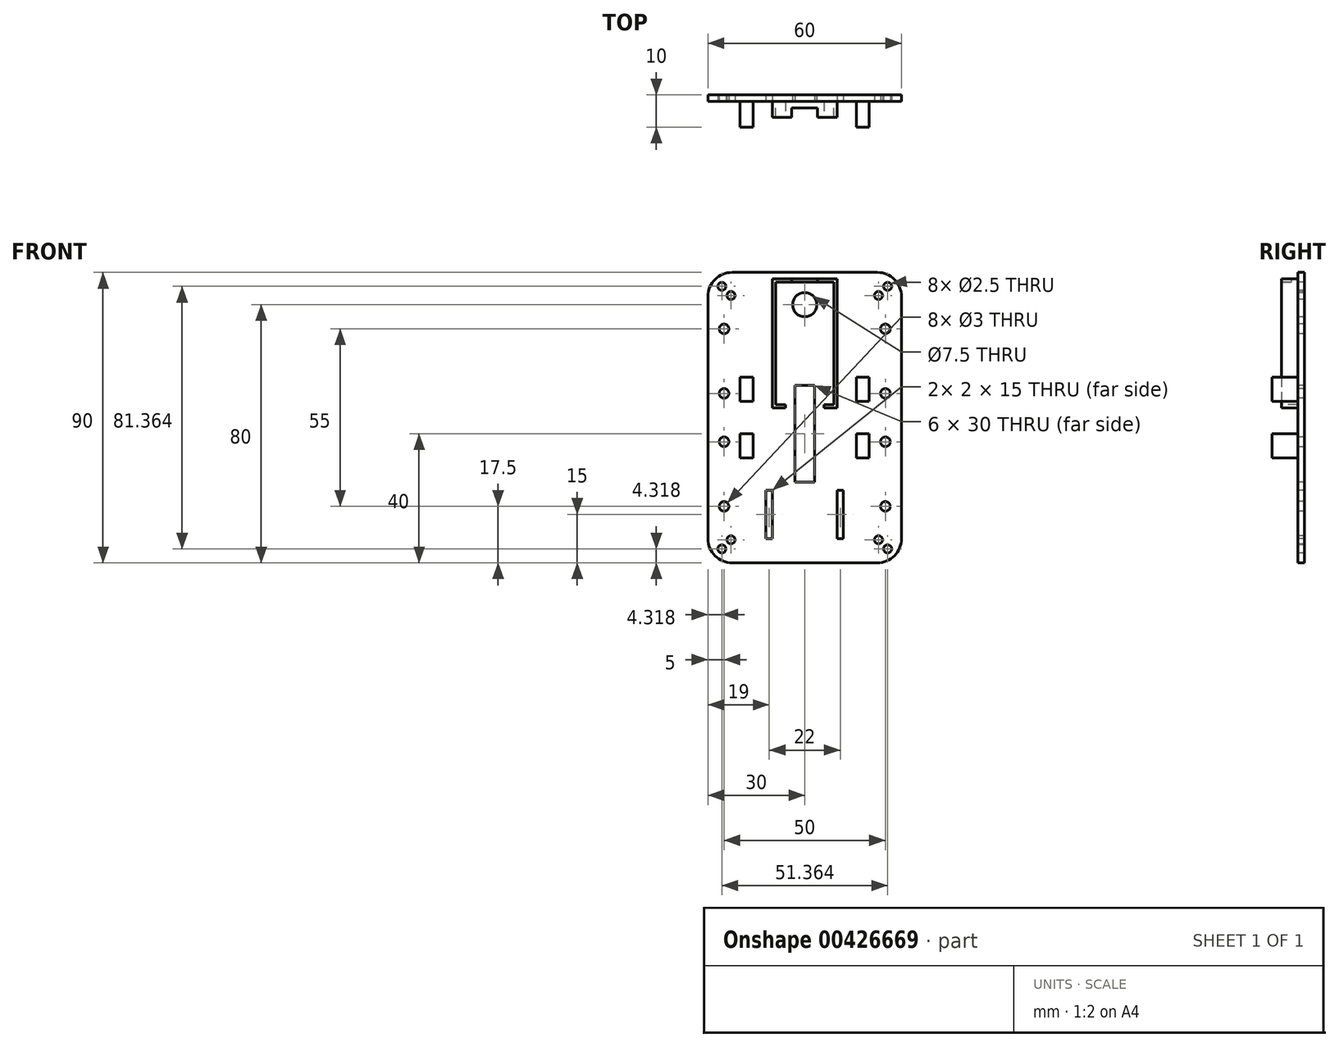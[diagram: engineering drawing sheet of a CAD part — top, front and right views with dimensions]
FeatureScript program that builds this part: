
annotation { "Feature Type Name" : "Feature", "Feature Type Description" : "" }
export const myFeature = defineFeature(function(context is Context, id is Id, definition is map)
    precondition{}
    {
        {
            var Q0;
            Q0=qCreatedBy(makeId("Front.planeOp"),FACE);
            var sketch = newSketch(context, id + "F0", { "sketchPlane" : qUnion([Q0])});
            skLineSegment(sketch, "E0.bottom", {"start": v(0, 0) * mm, "end": v(60, 0) * mm});
            skLineSegment(sketch, "E0.top", {"start": v(0, 90) * mm, "end": v(60, 90) * mm});
            skLineSegment(sketch, "E0.left", {"start": v(0, 0) * mm, "end": v(0, 90) * mm});
            skLineSegment(sketch, "E0.right", {"start": v(60, 0) * mm, "end": v(60, 90) * mm});
            skSolve(sketch);
        }
        {
            var Q0;
            Q0 = qSketchRegion(id + "F0", true);
            extrude(context, id + "F1", {"entities" : qUnion([Q0]), "depth" : 2 * mm, "offsetDistance" : 25 * mm});
        }
        {
            var Q0;
            Q0=makeQuery(id+"F1.opExtrude","SWEPT_EDGE",EDGE,{"disambiguationData":[OSD([sQuery(id+"F0.wireOp",EDGE,"E0.top"),sQuery(id+"F0.wireOp",EDGE,"E0.left")])]});
            var Q1;
            Q1=makeQuery(id+"F1.opExtrude","SWEPT_EDGE",EDGE,{"disambiguationData":[OSD([sQuery(id+"F0.wireOp",EDGE,"E0.top"),sQuery(id+"F0.wireOp",EDGE,"E0.right")])]});
            var Q2;
            Q2=makeQuery(id+"F1.opExtrude","SWEPT_EDGE",EDGE,{"disambiguationData":[OSD([sQuery(id+"F0.wireOp",EDGE,"E0.bottom"),sQuery(id+"F0.wireOp",EDGE,"E0.right")])]});
            var Q3;
            Q3=makeQuery(id+"F1.opExtrude","SWEPT_EDGE",EDGE,{"disambiguationData":[OSD([sQuery(id+"F0.wireOp",EDGE,"E0.bottom"),sQuery(id+"F0.wireOp",EDGE,"E0.left")])]});
            fillet(context, id + "F2", {"entities" : qUnion([Q0, Q1, Q2, Q3]), "radius" : 7.5 * mm, "tangentPropagation" : true, "allowEdgeOverflow" : false});
        }
        {
            var Q0;
            Q0=makeQuery(id+"F1.opExtrude","CAP_FACE",FACE,{"disambiguationData":[OSD([sQuery(id+"F0.wireOp",EDGE,"E0.bottom"),sQuery(id+"F0.wireOp",EDGE,"E0.top"),sQuery(id+"F0.wireOp",EDGE,"E0.left"),sQuery(id+"F0.wireOp",EDGE,"E0.right")])],"isStart":false});
            var sketch = newSketch(context, id + "F3", { "sketchPlane" : qUnion([Q0])});
            skSolve(sketch);
        }
        {
            var Q0;
            Q0=makeQuery(id+"F1.opExtrude","CAP_FACE",FACE,{"disambiguationData":[OSD([sQuery(id+"F0.wireOp",EDGE,"E0.bottom"),sQuery(id+"F0.wireOp",EDGE,"E0.top"),sQuery(id+"F0.wireOp",EDGE,"E0.left"),sQuery(id+"F0.wireOp",EDGE,"E0.right")])],"isStart":false});
            var sketch = newSketch(context, id + "F4", { "sketchPlane" : qUnion([Q0])});
            skLineSegment(sketch, "E1.bottom", {"start": v(18, 22.5) * mm, "end": v(20, 22.5) * mm});
            skLineSegment(sketch, "E1.top", {"start": v(18, 7.5) * mm, "end": v(20, 7.5) * mm});
            skLineSegment(sketch, "E1.left", {"start": v(18, 22.5) * mm, "end": v(18, 7.5) * mm});
            skLineSegment(sketch, "E1.right", {"start": v(20, 22.5) * mm, "end": v(20, 7.5) * mm});
            skLineSegment(sketch, "E2.bottom", {"start": v(42, 22.5) * mm, "end": v(40, 22.5) * mm});
            skLineSegment(sketch, "E2.top", {"start": v(42, 7.5) * mm, "end": v(40, 7.5) * mm});
            skLineSegment(sketch, "E2.left", {"start": v(42, 22.5) * mm, "end": v(42, 7.5) * mm});
            skLineSegment(sketch, "E2.right", {"start": v(40, 22.5) * mm, "end": v(40, 7.5) * mm});
            skSolve(sketch);
        }
        {
            var Q0;
            Q0 = qSketchRegion(id + "F4", true);
            extrude(context, id + "F5", {"entities" : qUnion([Q0]), "operationType" : NewBodyOperationType.REMOVE, "oppositeDirection" : true, "depth" : 25 * mm});
        }
        {
            var Q0;
            Q0=makeQuery(id+"F1.opExtrude","CAP_FACE",FACE,{"disambiguationData":[OSD([sQuery(id+"F0.wireOp",EDGE,"E0.bottom"),sQuery(id+"F0.wireOp",EDGE,"E0.top"),sQuery(id+"F0.wireOp",EDGE,"E0.left"),sQuery(id+"F0.wireOp",EDGE,"E0.right")])],"isStart":false});
            var sketch = newSketch(context, id + "F6", { "sketchPlane" : qUnion([Q0])});
            skLineSegment(sketch, "E3.bottom", {"start": v(21, 87) * mm, "end": v(39, 87) * mm});
            skLineSegment(sketch, "E3.top", {"start": v(21, 49) * mm, "end": v(39, 49) * mm});
            skLineSegment(sketch, "E3.left", {"start": v(21, 87) * mm, "end": v(21, 49) * mm});
            skLineSegment(sketch, "E3.right", {"start": v(39, 87) * mm, "end": v(39, 49) * mm});
            skLineSegment(sketch, "E4.bottom", {"start": v(20, 88) * mm, "end": v(40, 88) * mm});
            skLineSegment(sketch, "E4.top", {"start": v(20, 48) * mm, "end": v(40, 48) * mm});
            skLineSegment(sketch, "E4.left", {"start": v(20, 88) * mm, "end": v(20, 48) * mm});
            skLineSegment(sketch, "E4.right", {"start": v(40, 88) * mm, "end": v(40, 48) * mm});
            skSolve(sketch);
        }
        {
            var Q0;
            Q0=makeQuery(id+"F6.imprint","IMPRINT",FACE,{"disambiguationData":[TD([[makeQuery(id+"F6.imprint","IMPRINT",EDGE,{"derivedFrom":sQuery(id+"F6.wireOp",EDGE,"E3.bottom")}),1.0]])]});
            extrude(context, id + "F7", {"entities" : qUnion([Q0]), "operationType" : NewBodyOperationType.ADD, "depth" : 5 * mm, "offsetDistance" : 25 * mm});
        }
        {
            var Q0;
            Q0=makeQuery(id+"F7.opExtrude","CAP_FACE",FACE,{"disambiguationData":[OSD([sQuery(id+"F6.wireOp",EDGE,"E3.bottom"),sQuery(id+"F6.wireOp",EDGE,"E3.top"),sQuery(id+"F6.wireOp",EDGE,"E3.left"),sQuery(id+"F6.wireOp",EDGE,"E3.right"),sQuery(id+"F6.wireOp",EDGE,"E4.bottom"),sQuery(id+"F6.wireOp",EDGE,"E4.top"),sQuery(id+"F6.wireOp",EDGE,"E4.left"),sQuery(id+"F6.wireOp",EDGE,"E4.right")])],"isStart":false});
            var sketch = newSketch(context, id + "F8", { "sketchPlane" : qUnion([Q0])});
            skLineSegment(sketch, "E5", {"start": v(26, 88) * mm, "end": v(26, 87) * mm});
            skLineSegment(sketch, "E6", {"start": v(26, 87) * mm, "end": v(34, 87) * mm});
            skLineSegment(sketch, "E7", {"start": v(34, 87) * mm, "end": v(34, 88) * mm});
            skLineSegment(sketch, "E8", {"start": v(34, 88) * mm, "end": v(26, 88) * mm});
            skSolve(sketch);
        }
        {
            var Q0;
            Q0 = qSketchRegion(id + "F8", true);
            extrude(context, id + "F9", {"entities" : qUnion([Q0]), "operationType" : NewBodyOperationType.REMOVE, "oppositeDirection" : true, "depth" : 3 * mm, "offsetDistance" : 25 * mm});
        }
        {
            var Q0;
            Q0=makeQuery(id+"F7.opExtrude","CAP_FACE",FACE,{"disambiguationData":[OSD([sQuery(id+"F6.wireOp",EDGE,"E3.bottom"),sQuery(id+"F6.wireOp",EDGE,"E3.top"),sQuery(id+"F6.wireOp",EDGE,"E3.left"),sQuery(id+"F6.wireOp",EDGE,"E3.right"),sQuery(id+"F6.wireOp",EDGE,"E4.bottom"),sQuery(id+"F6.wireOp",EDGE,"E4.top"),sQuery(id+"F6.wireOp",EDGE,"E4.left"),sQuery(id+"F6.wireOp",EDGE,"E4.right")])],"isStart":false});
            var sketch = newSketch(context, id + "F10", { "sketchPlane" : qUnion([Q0])});
            skLineSegment(sketch, "E9", {"start": v(24, 49) * mm, "end": v(24, 48) * mm});
            skLineSegment(sketch, "E10", {"start": v(24, 48) * mm, "end": v(36, 48) * mm});
            skLineSegment(sketch, "E11", {"start": v(36, 48) * mm, "end": v(36, 49) * mm});
            skLineSegment(sketch, "E12", {"start": v(36, 49) * mm, "end": v(24, 49) * mm});
            skSolve(sketch);
        }
        {
            var Q0;
            Q0 = qSketchRegion(id + "F10", true);
            extrude(context, id + "F11", {"entities" : qUnion([Q0]), "operationType" : NewBodyOperationType.REMOVE, "oppositeDirection" : true, "depth" : 5 * mm, "offsetDistance" : 25 * mm});
        }
        {
            var Q0;
            {var subQ0=sQuery(id+"F0.wireOp",EDGE,"E0.right");var subQ1=sQuery(id+"F0.wireOp",EDGE,"E0.left");var subQ2=sQuery(id+"F0.wireOp",EDGE,"E0.top");var subQ3=sQuery(id+"F0.wireOp",EDGE,"E0.bottom");var subQ4=makeQuery(id+"F1.opExtrude","CAP_FACE",FACE,{"disambiguationData":[OSD([subQ3,subQ2,subQ1,subQ0])],"isStart":false});Q0=makeQuery(id+"F11.boolean.opBoolean","MERGE",FACE,{"derivedFrom":[makeQuery(id+"F7.boolean.opBoolean","SPLIT",FACE,{"disambiguationData":[TD([makeQuery(id+"F1.opExtrude","SWEPT_FACE",FACE,{"disambiguationData":[OSD([subQ3])]})])],"derivedFrom":subQ4}),makeQuery(id+"F7.boolean.opBoolean","SPLIT",FACE,{"disambiguationData":[TD([makeQuery(id+"F7.opExtrude","SWEPT_FACE",FACE,{"disambiguationData":[OSD([sQuery(id+"F6.wireOp",EDGE,"E3.bottom")])]})])],"derivedFrom":subQ4}),makeQuery(id+"F11.opExtrude","CAP_FACE",FACE,{"disambiguationData":[OSD([sQuery(id+"F10.wireOp",EDGE,"E9"),sQuery(id+"F10.wireOp",EDGE,"E10"),sQuery(id+"F10.wireOp",EDGE,"E11"),sQuery(id+"F10.wireOp",EDGE,"E12")])],"isStart":false})]});}
            var sketch = newSketch(context, id + "F12", { "sketchPlane" : qUnion([Q0])});
            skCircle(sketch, "E13", {"center": v(7.15, 82.85) * mm, "radius": 1.25 * mm});
            skCircle(sketch, "E14", {"center": v(52.85, 82.85) * mm, "radius": 1.25 * mm});
            skCircle(sketch, "E15", {"center": v(55.68, 4.32) * mm, "radius": 1.25 * mm});
            skCircle(sketch, "E16", {"center": v(4.32, 4.32) * mm, "radius": 1.25 * mm});
            skCircle(sketch, "E17", {"center": v(7.15, 7.15) * mm, "radius": 1.25 * mm});
            skCircle(sketch, "E18", {"center": v(52.85, 7.15) * mm, "radius": 1.25 * mm});
            skCircle(sketch, "E19", {"center": v(55.68, 85.68) * mm, "radius": 1.25 * mm});
            skCircle(sketch, "E20", {"center": v(4.32, 85.68) * mm, "radius": 1.25 * mm});
            skPoint(sketch, "E21.orphan", {"position": v(0, 7.5) * mm});
            skPoint(sketch, "E22.trimOffspring.end.orphan", {"position": v(7.5, 7.5) * mm});
            skPoint(sketch, "E23.start.orphan", {"position": v(2.2, 2.2) * mm});
            skPoint(sketch, "E24.start.orphan", {"position": v(57.8, 2.2) * mm});
            skPoint(sketch, "E25.trimOffspring.end.orphan", {"position": v(52.5, 7.5) * mm});
            skPoint(sketch, "E26.start.orphan", {"position": v(57.8, 87.8) * mm});
            skPoint(sketch, "E27.trimOffspring.end.orphan", {"position": v(52.5, 82.5) * mm});
            skPoint(sketch, "E28.start.orphan", {"position": v(2.2, 87.8) * mm});
            skPoint(sketch, "E29.trimOffspring.end.orphan", {"position": v(7.5, 82.5) * mm});
            skSolve(sketch);
        }
        {
            var Q0;
            Q0 = qSketchRegion(id + "F12", true);
            extrude(context, id + "F13", {"entities" : qUnion([Q0]), "operationType" : NewBodyOperationType.REMOVE, "oppositeDirection" : true, "depth" : 25 * mm, "offsetDistance" : 25 * mm});
        }
        {
            var Q0;
            {var subQ3=sQuery(id+"F0.wireOp",EDGE,"E0.bottom");Q0=makeQuery(id+"F3.imprint","IMPRINT",FACE,{"disambiguationData":[TD([[makeQuery(id+"F3.imprint","IMPRINT",EDGE,{"derivedFrom":makeQuery(id+"F1.opExtrude","CAP_EDGE",EDGE,{"disambiguationData":[OSD([subQ3])],"isStart":false})}),1.0]])]});}
            var sketch = newSketch(context, id + "F14", { "sketchPlane" : qUnion([Q0])});
            skLineSegment(sketch, "E30.bottom", {"start": v(27, 55) * mm, "end": v(33, 55) * mm});
            skLineSegment(sketch, "E30.top", {"start": v(27, 25) * mm, "end": v(33, 25) * mm});
            skLineSegment(sketch, "E30.left", {"start": v(27, 55) * mm, "end": v(27, 25) * mm});
            skLineSegment(sketch, "E30.right", {"start": v(33, 55) * mm, "end": v(33, 25) * mm});
            skSolve(sketch);
        }
        {
            var Q0;
            Q0 = qSketchRegion(id + "F14", true);
            extrude(context, id + "F15", {"entities" : qUnion([Q0]), "operationType" : NewBodyOperationType.REMOVE, "oppositeDirection" : true, "depth" : 25 * mm, "offsetDistance" : 25 * mm});
        }
        {
            var Q0;
            {var subQ3=sQuery(id+"F0.wireOp",EDGE,"E0.bottom");Q0=makeQuery(id+"F3.imprint","IMPRINT",FACE,{"disambiguationData":[TD([[makeQuery(id+"F3.imprint","IMPRINT",EDGE,{"derivedFrom":makeQuery(id+"F1.opExtrude","CAP_EDGE",EDGE,{"disambiguationData":[OSD([subQ3])],"isStart":false})}),1.0]])]});}
            var sketch = newSketch(context, id + "F16", { "sketchPlane" : qUnion([Q0])});
            skCircle(sketch, "E31", {"center": v(30, 80) * mm, "radius": 3.75 * mm});
            skSolve(sketch);
        }
        {
            var Q0;
            Q0 = qSketchRegion(id + "F16", true);
            extrude(context, id + "F17", {"entities" : qUnion([Q0]), "operationType" : NewBodyOperationType.REMOVE, "oppositeDirection" : true, "depth" : 25 * mm, "offsetDistance" : 25 * mm});
        }
        {
            var Q0;
            {var subQ3=sQuery(id+"F0.wireOp",EDGE,"E0.bottom");Q0=makeQuery(id+"F3.imprint","IMPRINT",FACE,{"disambiguationData":[TD([[makeQuery(id+"F3.imprint","IMPRINT",EDGE,{"derivedFrom":makeQuery(id+"F1.opExtrude","CAP_EDGE",EDGE,{"disambiguationData":[OSD([subQ3])],"isStart":false})}),1.0]])]});}
            var sketch = newSketch(context, id + "F18", { "sketchPlane" : qUnion([Q0])});
            skCircle(sketch, "E32", {"center": v(5, 17.5) * mm, "radius": 1.5 * mm});
            skCircle(sketch, "E33", {"center": v(5, 72.5) * mm, "radius": 1.5 * mm});
            skCircle(sketch, "E34", {"center": v(55, 72.5) * mm, "radius": 1.5 * mm});
            skCircle(sketch, "E35", {"center": v(55, 17.5) * mm, "radius": 1.5 * mm});
            skSolve(sketch);
        }
        {
            var Q0;
            Q0 = qSketchRegion(id + "F18", true);
            extrude(context, id + "F19", {"entities" : qUnion([Q0]), "operationType" : NewBodyOperationType.REMOVE, "oppositeDirection" : true, "depth" : 25 * mm, "offsetDistance" : 25 * mm});
        }
        {
            var Q0;
            {var subQ3=sQuery(id+"F0.wireOp",EDGE,"E0.bottom");Q0=makeQuery(id+"F3.imprint","IMPRINT",FACE,{"disambiguationData":[TD([[makeQuery(id+"F3.imprint","IMPRINT",EDGE,{"derivedFrom":makeQuery(id+"F1.opExtrude","CAP_EDGE",EDGE,{"disambiguationData":[OSD([subQ3])],"isStart":false})}),1.0]])]});}
            var sketch = newSketch(context, id + "F20", { "sketchPlane" : qUnion([Q0])});
            skLineSegment(sketch, "E36.bottom", {"start": v(10, 57.5) * mm, "end": v(14, 57.5) * mm});
            skLineSegment(sketch, "E36.top", {"start": v(10, 32.5) * mm, "end": v(14, 32.5) * mm});
            skLineSegment(sketch, "E36.left", {"start": v(10, 57.5) * mm, "end": v(10, 32.5) * mm});
            skLineSegment(sketch, "E36.right", {"start": v(14, 57.5) * mm, "end": v(14, 32.5) * mm});
            skLineSegment(sketch, "E37.bottom", {"start": v(46, 57.5) * mm, "end": v(50, 57.5) * mm});
            skLineSegment(sketch, "E37.top", {"start": v(46, 32.5) * mm, "end": v(50, 32.5) * mm});
            skLineSegment(sketch, "E37.left", {"start": v(46, 57.5) * mm, "end": v(46, 32.5) * mm});
            skLineSegment(sketch, "E37.right", {"start": v(50, 57.5) * mm, "end": v(50, 32.5) * mm});
            skSolve(sketch);
        }
        {
            var Q0;
            Q0 = qSketchRegion(id + "F20", true);
            extrude(context, id + "F21", {"entities" : qUnion([Q0]), "operationType" : NewBodyOperationType.ADD, "depth" : 8 * mm, "offsetDistance" : 25 * mm});
        }
        {
            var Q0;
            {var subQ3=sQuery(id+"F0.wireOp",EDGE,"E0.bottom");Q0=makeQuery(id+"F3.imprint","IMPRINT",FACE,{"disambiguationData":[TD([[makeQuery(id+"F3.imprint","IMPRINT",EDGE,{"derivedFrom":makeQuery(id+"F1.opExtrude","CAP_EDGE",EDGE,{"disambiguationData":[OSD([subQ3])],"isStart":false})}),1.0]])]});}
            var sketch = newSketch(context, id + "F22", { "sketchPlane" : qUnion([Q0])});
            skCircle(sketch, "E38", {"center": v(5, 52.5) * mm, "radius": 1.5 * mm});
            skCircle(sketch, "E39", {"center": v(5, 37.5) * mm, "radius": 1.5 * mm});
            skCircle(sketch, "E40", {"center": v(55, 52.5) * mm, "radius": 1.5 * mm});
            skCircle(sketch, "E41", {"center": v(55, 37.5) * mm, "radius": 1.5 * mm});
            skSolve(sketch);
        }
        {
            var Q0;
            Q0 = qSketchRegion(id + "F22", true);
            extrude(context, id + "F23", {"entities" : qUnion([Q0]), "operationType" : NewBodyOperationType.REMOVE, "oppositeDirection" : true, "depth" : 25 * mm, "offsetDistance" : 25 * mm});
        }
        {
            var Q0;
            Q0=makeQuery(id+"F21.opExtrude","CAP_FACE",FACE,{"disambiguationData":[OSD([sQuery(id+"F20.wireOp",EDGE,"E36.bottom"),sQuery(id+"F20.wireOp",EDGE,"E36.top"),sQuery(id+"F20.wireOp",EDGE,"E36.left"),sQuery(id+"F20.wireOp",EDGE,"E36.right")])],"isStart":false});
            var sketch = newSketch(context, id + "F24", { "sketchPlane" : qUnion([Q0])});
            skLineSegment(sketch, "E42.bottom", {"start": v(10, 50) * mm, "end": v(14, 50) * mm});
            skLineSegment(sketch, "E42.top", {"start": v(10, 40) * mm, "end": v(14, 40) * mm});
            skLineSegment(sketch, "E42.left", {"start": v(10, 50) * mm, "end": v(10, 40) * mm});
            skLineSegment(sketch, "E42.right", {"start": v(14, 50) * mm, "end": v(14, 40) * mm});
            skLineSegment(sketch, "E43.bottom", {"start": v(46, 50) * mm, "end": v(50, 50) * mm});
            skLineSegment(sketch, "E43.top", {"start": v(46, 40) * mm, "end": v(50, 40) * mm});
            skLineSegment(sketch, "E43.left", {"start": v(46, 50) * mm, "end": v(46, 40) * mm});
            skLineSegment(sketch, "E43.right", {"start": v(50, 50) * mm, "end": v(50, 40) * mm});
            skSolve(sketch);
        }
        {
            var Q0;
            Q0 = qSketchRegion(id + "F24", true);
            extrude(context, id + "F25", {"entities" : qUnion([Q0]), "operationType" : NewBodyOperationType.REMOVE, "oppositeDirection" : true, "depth" : 8 * mm, "offsetDistance" : 25 * mm});
        }
    });
